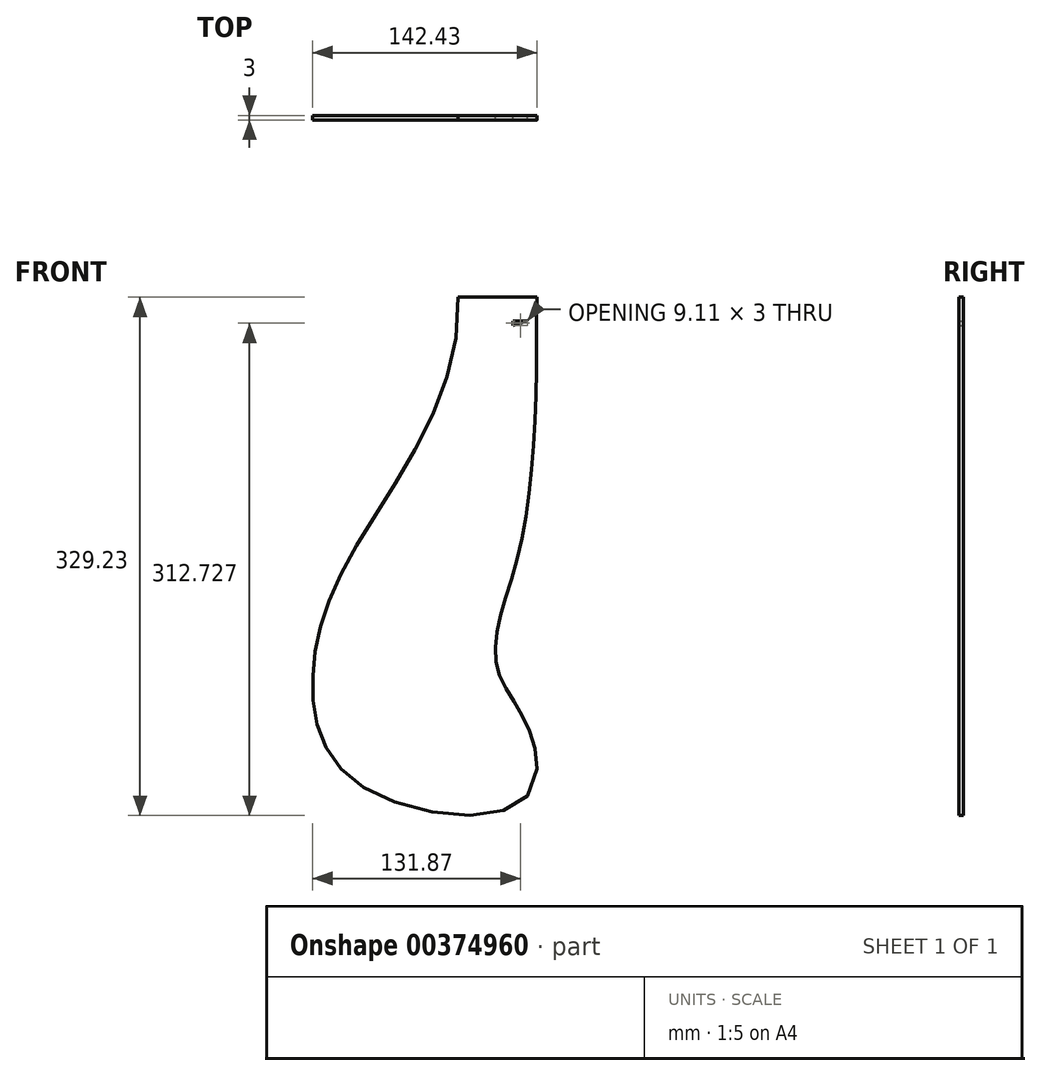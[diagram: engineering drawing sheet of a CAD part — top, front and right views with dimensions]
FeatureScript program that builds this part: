
annotation { "Feature Type Name" : "Feature", "Feature Type Description" : "" }
export const myFeature = defineFeature(function(context is Context, id is Id, definition is map)
    precondition{}
    {
        {
            var Q0;
            Q0=qCreatedBy(makeId("Front.planeOp"),FACE);
            var sketch = newSketch(context, id + "F0", { "sketchPlane" : qUnion([Q0])});
            skLineSegment(sketch, "E0", {"start": v(0, 63.2) * mm, "end": v(-50, 63.2) * mm});
            skFitSpline(sketch, "E1", {"points": [v(-50, 63.2) * mm, v(-118.1, -100.93) * mm, v(-142.33, -185.74) * mm, v(-103.81, -251.63) * mm, v(0.06, -236.5) * mm], "startDerivative": vector(29.55, -605.71) * mm, "endDerivative": vector(0.71, 483.65) * mm});
            skLineSegment(sketch, "E2", {"start": v(0, 63.2) * mm, "end": v(-0.05, 48.2) * mm});
            skLineSegment(sketch, "E3", {"start": v(-0.05, 48.2) * mm, "end": v(-15.05, 48.2) * mm});
            skLineSegment(sketch, "E4", {"start": v(-15.05, 48.2) * mm, "end": v(-15.05, 45.2) * mm});
            skLineSegment(sketch, "E5", {"start": v(-15.05, 45.2) * mm, "end": v(-0.05, 50.14) * mm});
            skFitSpline(sketch, "E6", {"points": [v(-0.05, 50.14) * mm, v(-11.08, -96.9) * mm, v(-25.2, -172.28) * mm, v(0.06, -236.5) * mm], "startDerivative": vector(0.4, -361.8) * mm, "endDerivative": vector(0.62, -327) * mm});
            skSolve(sketch);
        }
        {
            var Q0;
            Q0 = qSketchRegion(id + "F0", true);
            extrude(context, id + "F1", {"entities" : qUnion([Q0]), "depth" : 3 * mm});
        }
    });
